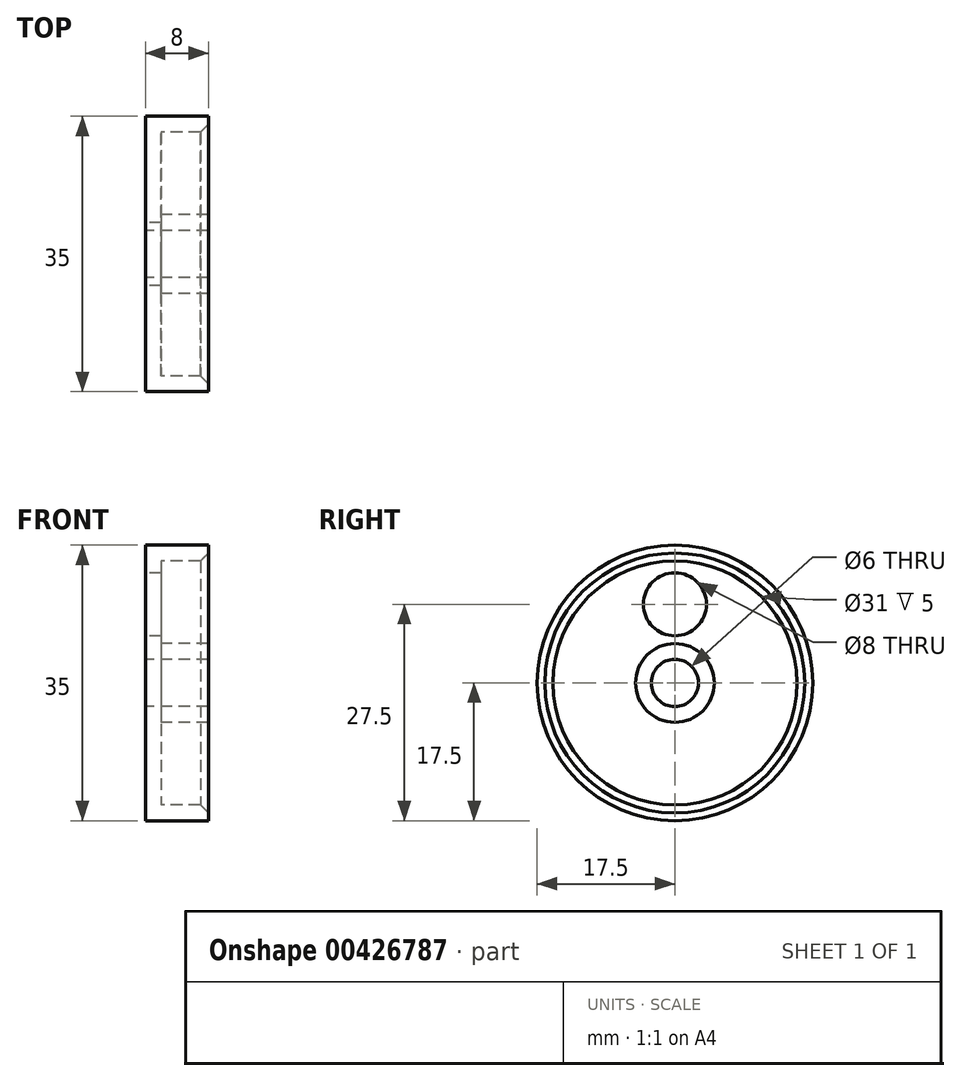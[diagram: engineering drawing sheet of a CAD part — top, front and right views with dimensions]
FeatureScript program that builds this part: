
annotation { "Feature Type Name" : "Feature", "Feature Type Description" : "" }
export const myFeature = defineFeature(function(context is Context, id is Id, definition is map)
    precondition{}
    {
        {
            var Q0;
            Q0=qCreatedBy(makeId("Top.planeOp"),FACE);
            var sketch = newSketch(context, id + "F0", { "sketchPlane" : qUnion([Q0])});
            skLineSegment(sketch, "E0.bottom", {"start": v(0, 0) * mm, "end": v(8, 0) * mm});
            skLineSegment(sketch, "E0.top", {"start": v(0, 17.5) * mm, "end": v(8, 17.5) * mm});
            skLineSegment(sketch, "E0.left", {"start": v(0, 0) * mm, "end": v(0, 17.5) * mm});
            skLineSegment(sketch, "E0.right", {"start": v(8, 0) * mm, "end": v(8, 17.5) * mm});
            skSolve(sketch);
        }
        {
            var Q0;
            Q0 = qSketchRegion(id + "F0", true);
            var Q1;
            Q1=sQuery(id+"F0.wireOp",EDGE,"E0.bottom");
            revolve(context, id + "F1", {"entities" : qUnion([Q0]), "axis" : qUnion([Q1]), "revolveType" : RevolveType.FULL});
        }
        {
            var Q0;
            Q0=qCreatedBy(makeId("Right.planeOp"),FACE);
            var sketch = newSketch(context, id + "F2", { "sketchPlane" : qUnion([Q0])});
            skPoint(sketch, "E1", {"position": v(0, 0) * mm});
            skSolve(sketch);
        }
        {
            var Q0;
            Q0=sQuery(id+"F2.wireOp",VERTEX,"E1");
            var Q1;
            Q1=makeQuery(id+"F1.opRevolve","SWEPT_BODY",BODY,{"disambiguationData":[OSD([sQuery(id+"F0.wireOp",EDGE,"E0.bottom"),sQuery(id+"F0.wireOp",EDGE,"E0.top"),sQuery(id+"F0.wireOp",EDGE,"E0.left"),sQuery(id+"F0.wireOp",EDGE,"E0.right")])]});
            hole(context, id + "F3", {"style" : HoleStyle.SIMPLE, "endStyle" : HoleEndStyle.THROUGH, "oppositeDirection" : true, "holeDiameter" : 6 * mm, "isTappedThrough" : true, "tappedDepth" : 12 * mm, "tapClearance" : 3, "locations" : qUnion([Q0]), "scope" : qUnion([Q1])});
        }
        {
            var Q0;
            Q0=makeQuery(id+"F1.opRevolve","SWEPT_FACE",FACE,{"disambiguationData":[OSD([sQuery(id+"F0.wireOp",EDGE,"E0.right")])]});
            shell(context, id + "F4", {"entities" : qUnion([Q0]), "thickness" : 2 * mm});
        }
        {
            var Q0;
            Q0=qCreatedBy(makeId("Right.planeOp"),FACE);
            var sketch = newSketch(context, id + "F5", { "sketchPlane" : qUnion([Q0])});
            skPoint(sketch, "E2", {"position": v(0, 10) * mm});
            skSolve(sketch);
        }
        {
            var Q0;
            Q0=sQuery(id+"F5.wireOp",VERTEX,"E2");
            var Q1;
            Q1=makeQuery(id+"F1.opRevolve","SWEPT_BODY",BODY,{"disambiguationData":[OSD([sQuery(id+"F0.wireOp",EDGE,"E0.bottom"),sQuery(id+"F0.wireOp",EDGE,"E0.top"),sQuery(id+"F0.wireOp",EDGE,"E0.left"),sQuery(id+"F0.wireOp",EDGE,"E0.right")])]});
            hole(context, id + "F6", {"style" : HoleStyle.SIMPLE, "endStyle" : HoleEndStyle.THROUGH, "oppositeDirection" : true, "holeDiameter" : 8 * mm, "isTappedThrough" : true, "tappedDepth" : 12 * mm, "tapClearance" : 3, "locations" : qUnion([Q0]), "scope" : qUnion([Q1])});
        }
        {
            var Q0;
            Q0=makeQuery(id+"F4.opShell","OFFSET_EDGE",EDGE,{"disambiguationData":[OSD([sQuery(id+"F0.wireOp",EDGE,"E0.top"),sQuery(id+"F0.wireOp",EDGE,"E0.right")])]});
            chamfer(context, id + "F7", {"entities" : qUnion([Q0]), "width" : 1 * mm, "tangentPropagation" : true});
        }
    });
